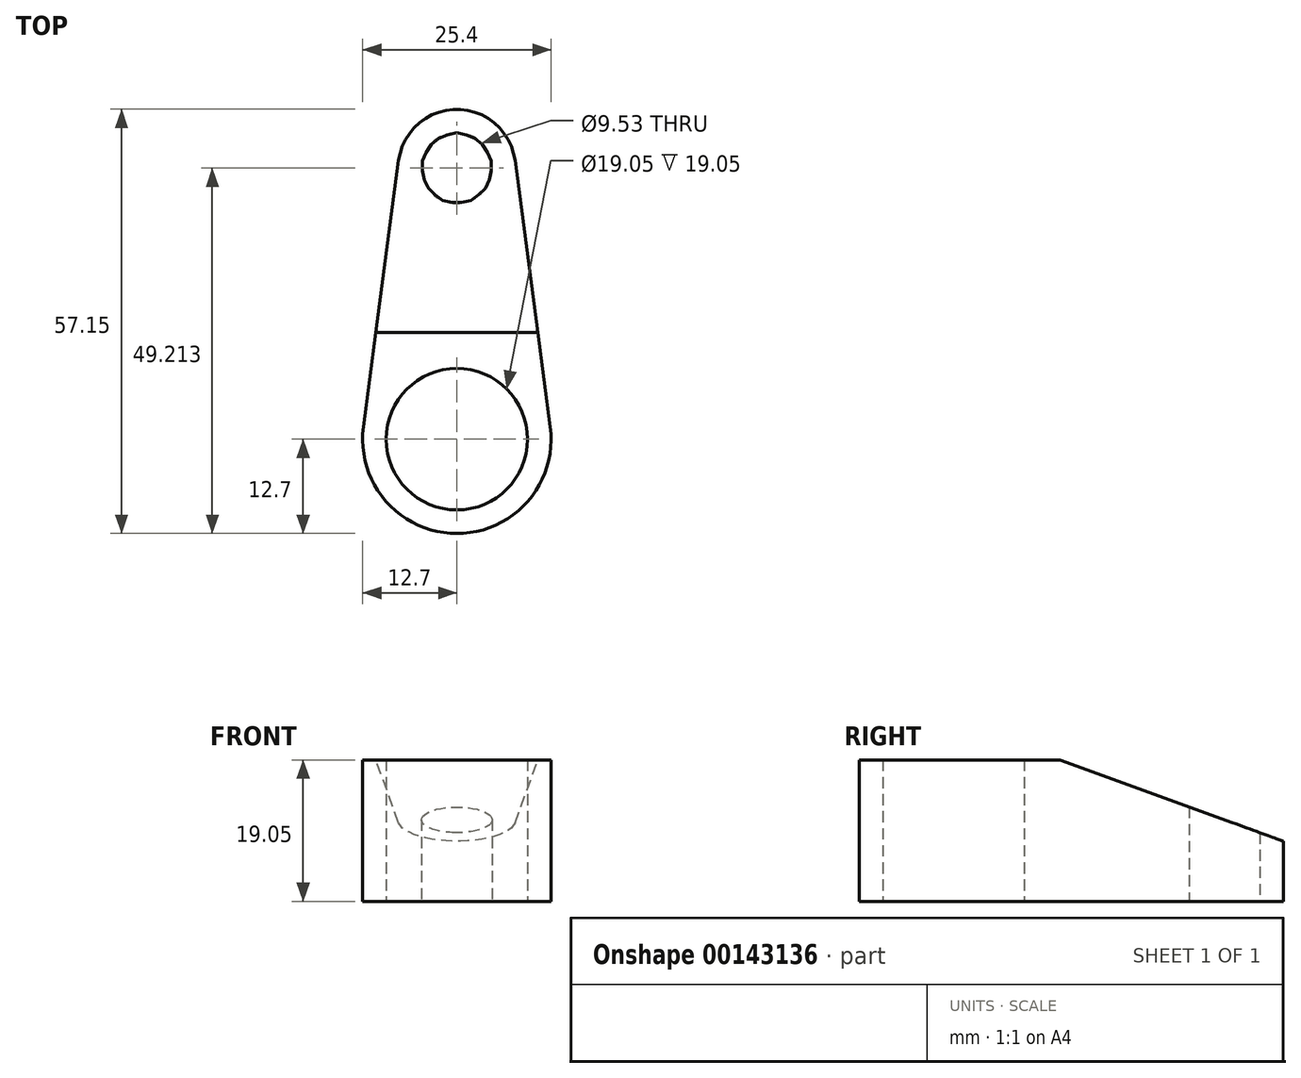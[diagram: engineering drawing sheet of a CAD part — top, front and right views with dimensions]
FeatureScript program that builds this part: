
annotation { "Feature Type Name" : "Feature", "Feature Type Description" : "" }
export const myFeature = defineFeature(function(context is Context, id is Id, definition is map)
    precondition{}
    {
        {
            var Q0;
            Q0=qCreatedBy(makeId("Top.planeOp"),FACE);
            var sketch = newSketch(context, id + "F0", { "sketchPlane" : qUnion([Q0])});
            skCircle(sketch, "E0", {"center": v(0, 0) * mm, "radius": 12.7 * mm});
            skCircle(sketch, "E1", {"center": v(0, 36.51) * mm, "radius": 7.94 * mm});
            skCircle(sketch, "E2", {"center": v(0, 0) * mm, "radius": 9.53 * mm});
            skCircle(sketch, "E3", {"center": v(0, 36.51) * mm, "radius": 4.76 * mm});
            skLineSegment(sketch, "E4", {"start": v(-7.87, 37.55) * mm, "end": v(-12.8, 0) * mm});
            skLineSegment(sketch, "E5", {"start": v(7.87, 37.55) * mm, "end": v(12.8, 0) * mm});
            skSolve(sketch);
        }
        {
            var Q0;
            Q0=makeQuery(id+"F0.imprint","IMPRINT",FACE,{"disambiguationData":[TD([[makeQuery(id+"F0.imprint","IMPRINT",EDGE,{"derivedFrom":sQuery(id+"F0.wireOp",EDGE,"E3")}),-1.0]])]});
            var Q1;
            {var subQ0=sQuery(id+"F0.wireOp",EDGE,"E4");var subQ1=sQuery(id+"F0.wireOp",EDGE,"E0");var subQ2=makeQuery(id+"F0.imprint","INTERSECT",VERTEX,{"derivedFrom":[subQ1,subQ0]});Q1=makeQuery(id+"F0.imprint","IMPRINT",FACE,{"disambiguationData":[TD([[makeQuery(id+"F0.imprint","IMPRINT",EDGE,{"disambiguationData":[TD([[subQ2,1.0]])],"derivedFrom":subQ1}),-1.0]])]});}
            var Q2;
            Q2=makeQuery(id+"F0.imprint","IMPRINT",FACE,{"disambiguationData":[TD([[makeQuery(id+"F0.imprint","IMPRINT",EDGE,{"derivedFrom":sQuery(id+"F0.wireOp",EDGE,"E2")}),-1.0]])]});
            extrude(context, id + "F1", {"entities" : qUnion([Q0, Q1, Q2]), "depth" : 19.05 * mm});
        }
        {
            var Q0;
            Q0=qCreatedBy(makeId("Right.planeOp"),FACE);
            var sketch = newSketch(context, id + "F2", { "sketchPlane" : qUnion([Q0])});
            skLineSegment(sketch, "E6", {"start": v(14.36, 19.05) * mm, "end": v(46.84, 19.05) * mm});
            skLineSegment(sketch, "E7", {"start": v(46.84, 19.05) * mm, "end": v(46.84, 7.23) * mm});
            skLineSegment(sketch, "E8", {"start": v(46.84, 7.23) * mm, "end": v(14.36, 19.05) * mm});
            skSolve(sketch);
        }
        {
            var Q0;
            Q0=makeQuery(id+"F2.imprint","IMPRINT",FACE,{"disambiguationData":[TD([[makeQuery(id+"F2.imprint","IMPRINT",EDGE,{"derivedFrom":sQuery(id+"F2.wireOp",EDGE,"E6")}),-1.0]])]});
            extrude(context, id + "F3", {"entities" : qUnion([Q0]), "operationType" : NewBodyOperationType.REMOVE, "endBound" : BoundingType.THROUGH_ALL, "oppositeDirection" : true, "depth" : 25.4 * mm, "hasSecondDirection" : true, "secondDirectionOppositeDirection" : false, "secondDirectionDepth" : 25.4 * mm});
        }
    });
